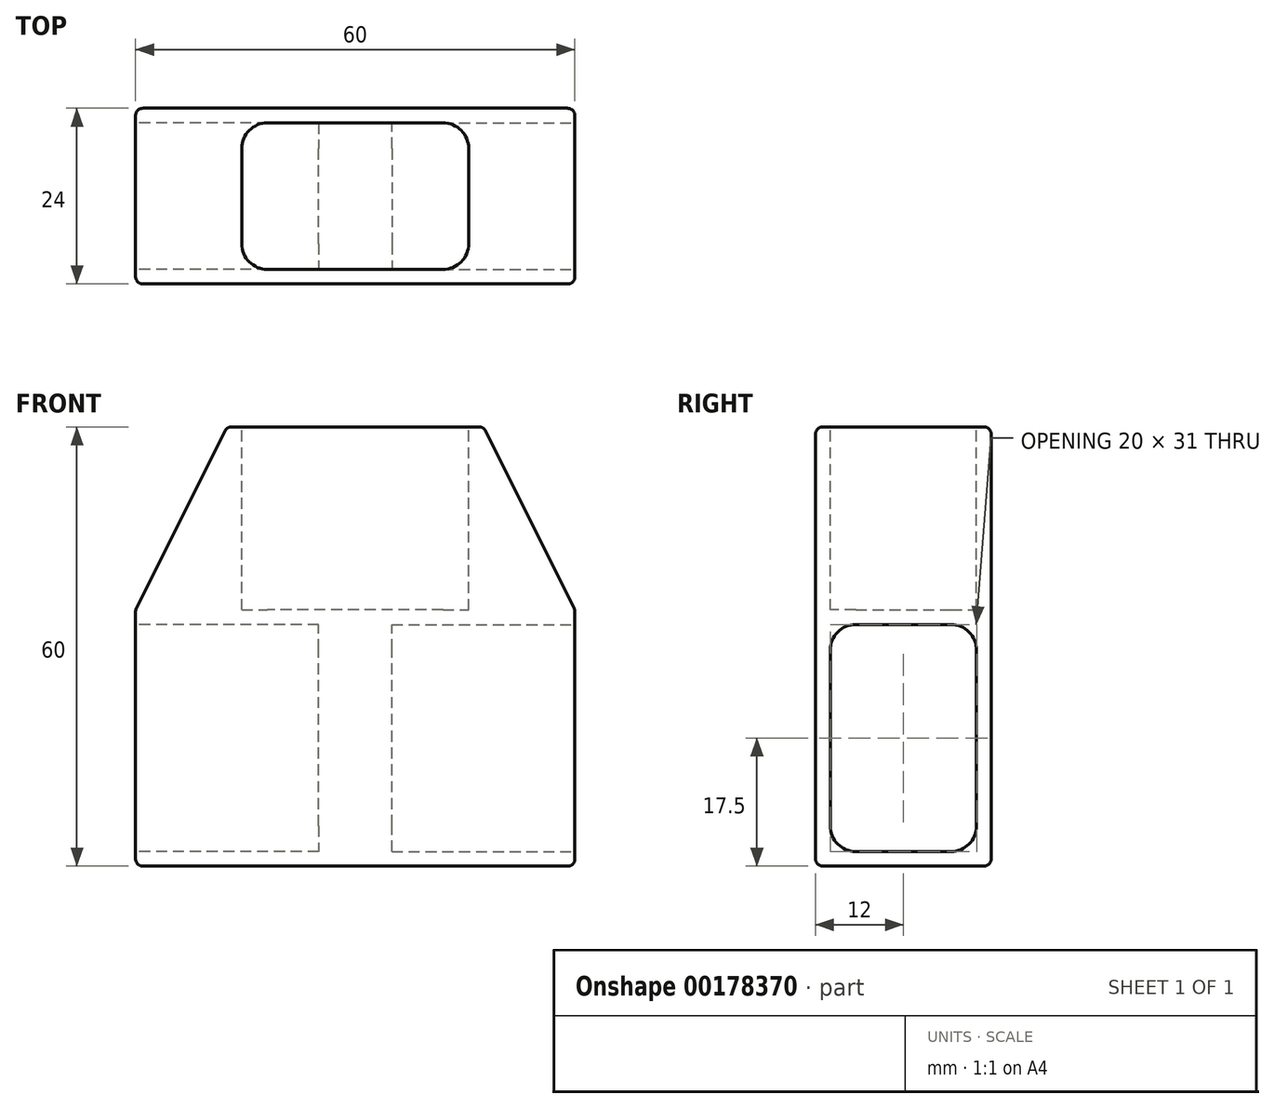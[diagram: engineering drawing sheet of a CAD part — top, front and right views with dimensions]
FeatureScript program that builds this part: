
annotation { "Feature Type Name" : "Feature", "Feature Type Description" : "" }
export const myFeature = defineFeature(function(context is Context, id is Id, definition is map)
    precondition{}
    {
        {
            var Q0;
            Q0=qCreatedBy(makeId("Top.planeOp"),FACE);
            var sketch = newSketch(context, id + "F0", { "sketchPlane" : qUnion([Q0])});
            skLineSegment(sketch, "E0.bottom", {"start": v(30, -12) * mm, "end": v(-30, -12) * mm});
            skLineSegment(sketch, "E0.top", {"start": v(30, 12) * mm, "end": v(-30, 12) * mm});
            skLineSegment(sketch, "E0.left", {"start": v(30, -12) * mm, "end": v(30, 12) * mm});
            skLineSegment(sketch, "E0.right", {"start": v(-30, -12) * mm, "end": v(-30, 12) * mm});
            skPoint(sketch, "E0.middle", {"position": v(0, 0) * mm});
            skSolve(sketch);
        }
        {
            var Q0;
            Q0=makeQuery(id+"F0.imprint","IMPRINT",FACE,{"disambiguationData":[TD([[makeQuery(id+"F0.imprint","IMPRINT",EDGE,{"derivedFrom":sQuery(id+"F0.wireOp",EDGE,"E0.bottom")}),-1.0]])]});
            extrude(context, id + "F1", {"entities" : qUnion([Q0]), "depth" : 60 * mm});
        }
        {
            var Q0;
            Q0=makeQuery(id+"F1.opExtrude","CAP_FACE",FACE,{"disambiguationData":[OSD([sQuery(id+"F0.wireOp",EDGE,"E0.bottom"),sQuery(id+"F0.wireOp",EDGE,"E0.top"),sQuery(id+"F0.wireOp",EDGE,"E0.left"),sQuery(id+"F0.wireOp",EDGE,"E0.right")])],"isStart":false});
            var sketch = newSketch(context, id + "F2", { "sketchPlane" : qUnion([Q0])});
            skLineSegment(sketch, "E1.bottom", {"start": v(15.5, -10) * mm, "end": v(-15.5, -10) * mm});
            skLineSegment(sketch, "E1.top", {"start": v(15.5, 10) * mm, "end": v(-15.5, 10) * mm});
            skLineSegment(sketch, "E1.left", {"start": v(15.5, -10) * mm, "end": v(15.5, 10) * mm});
            skLineSegment(sketch, "E1.right", {"start": v(-15.5, -10) * mm, "end": v(-15.5, 10) * mm});
            skPoint(sketch, "E1.middle", {"position": v(0, 0) * mm});
            skSolve(sketch);
        }
        {
            var Q0;
            Q0=makeQuery(id+"F1.opExtrude","SWEPT_FACE",FACE,{"disambiguationData":[OSD([sQuery(id+"F0.wireOp",EDGE,"E0.left")])]});
            var sketch = newSketch(context, id + "F3", { "sketchPlane" : qUnion([Q0])});
            skLineSegment(sketch, "E2.bottom", {"start": v(10, 2) * mm, "end": v(-10, 2) * mm});
            skLineSegment(sketch, "E2.top", {"start": v(10, 33) * mm, "end": v(-10, 33) * mm});
            skLineSegment(sketch, "E2.left", {"start": v(10, 2) * mm, "end": v(10, 33) * mm});
            skLineSegment(sketch, "E2.right", {"start": v(-10, 2) * mm, "end": v(-10, 33) * mm});
            skPoint(sketch, "E2.middle", {"position": v(0, 17.5) * mm});
            skSolve(sketch);
        }
        {
            var Q0;
            Q0=makeQuery(id+"F1.opExtrude","SWEPT_FACE",FACE,{"disambiguationData":[OSD([sQuery(id+"F0.wireOp",EDGE,"E0.right")])]});
            var sketch = newSketch(context, id + "F4", { "sketchPlane" : qUnion([Q0])});
            skLineSegment(sketch, "E3.bottom", {"start": v(10, 2) * mm, "end": v(-10, 2) * mm});
            skLineSegment(sketch, "E3.top", {"start": v(10, 33) * mm, "end": v(-10, 33) * mm});
            skLineSegment(sketch, "E3.left", {"start": v(10, 2) * mm, "end": v(10, 33) * mm});
            skLineSegment(sketch, "E3.right", {"start": v(-10, 2) * mm, "end": v(-10, 33) * mm});
            skPoint(sketch, "E3.middle", {"position": v(0, 17.5) * mm});
            skSolve(sketch);
        }
        {
            var Q0;
            Q0=makeQuery(id+"F2.imprint","IMPRINT",FACE,{"disambiguationData":[TD([[makeQuery(id+"F2.imprint","IMPRINT",EDGE,{"derivedFrom":sQuery(id+"F2.wireOp",EDGE,"E1.bottom")}),-1.0]])]});
            extrude(context, id + "F5", {"entities" : qUnion([Q0]), "operationType" : NewBodyOperationType.REMOVE, "oppositeDirection" : true, "depth" : 25 * mm});
        }
        {
            var Q0;
            Q0=makeQuery(id+"F4.imprint","IMPRINT",FACE,{"disambiguationData":[TD([[makeQuery(id+"F4.imprint","IMPRINT",EDGE,{"derivedFrom":sQuery(id+"F4.wireOp",EDGE,"E3.bottom")}),-1.0]])]});
            extrude(context, id + "F6", {"entities" : qUnion([Q0]), "operationType" : NewBodyOperationType.REMOVE, "oppositeDirection" : true, "depth" : 25 * mm});
        }
        {
            var Q0;
            Q0=makeQuery(id+"F3.imprint","IMPRINT",FACE,{"disambiguationData":[TD([[makeQuery(id+"F3.imprint","IMPRINT",EDGE,{"derivedFrom":sQuery(id+"F3.wireOp",EDGE,"E2.bottom")}),-1.0]])]});
            extrude(context, id + "F7", {"entities" : qUnion([Q0]), "operationType" : NewBodyOperationType.REMOVE, "oppositeDirection" : true, "depth" : 25 * mm});
        }
        {
            var Q0;
            Q0=makeQuery(id+"F1.opExtrude","CAP_EDGE",EDGE,{"disambiguationData":[OSD([sQuery(id+"F0.wireOp",EDGE,"E0.left")])],"isStart":false});
            var Q1;
            Q1=makeQuery(id+"F1.opExtrude","CAP_EDGE",EDGE,{"disambiguationData":[OSD([sQuery(id+"F0.wireOp",EDGE,"E0.right")])],"isStart":false});
            chamfer(context, id + "F8", {"entities" : qUnion([Q0, Q1]), "chamferType" : ChamferType.TWO_OFFSETS, "width1" : 12.5 * mm, "oppositeDirection" : false, "width2" : 25 * mm, "tangentPropagation" : true});
        }
        {
            var Q0;
            Q0=makeQuery(id+"F6.boolean.opBoolean","COPY",EDGE,{"derivedFrom":makeQuery(id+"F6.opExtrude","SWEPT_EDGE",EDGE,{"disambiguationData":[OSD([sQuery(id+"F4.wireOp",EDGE,"E3.top"),sQuery(id+"F4.wireOp",EDGE,"E3.right")])]})});
            var Q1;
            Q1=makeQuery(id+"F6.boolean.opBoolean","COPY",EDGE,{"derivedFrom":makeQuery(id+"F6.opExtrude","SWEPT_EDGE",EDGE,{"disambiguationData":[OSD([sQuery(id+"F4.wireOp",EDGE,"E3.top"),sQuery(id+"F4.wireOp",EDGE,"E3.left")])]})});
            var Q2;
            Q2=makeQuery(id+"F6.boolean.opBoolean","COPY",EDGE,{"derivedFrom":makeQuery(id+"F6.opExtrude","SWEPT_EDGE",EDGE,{"disambiguationData":[OSD([sQuery(id+"F4.wireOp",EDGE,"E3.bottom"),sQuery(id+"F4.wireOp",EDGE,"E3.left")])]})});
            var Q3;
            Q3=makeQuery(id+"F6.boolean.opBoolean","COPY",EDGE,{"derivedFrom":makeQuery(id+"F6.opExtrude","SWEPT_EDGE",EDGE,{"disambiguationData":[OSD([sQuery(id+"F4.wireOp",EDGE,"E3.bottom"),sQuery(id+"F4.wireOp",EDGE,"E3.right")])]})});
            var Q4;
            Q4=makeQuery(id+"F5.boolean.opBoolean","COPY",EDGE,{"derivedFrom":makeQuery(id+"F5.opExtrude","SWEPT_EDGE",EDGE,{"disambiguationData":[OSD([sQuery(id+"F2.wireOp",EDGE,"E1.bottom"),sQuery(id+"F2.wireOp",EDGE,"E1.left")])]})});
            var Q5;
            Q5=makeQuery(id+"F5.boolean.opBoolean","COPY",EDGE,{"derivedFrom":makeQuery(id+"F5.opExtrude","SWEPT_EDGE",EDGE,{"disambiguationData":[OSD([sQuery(id+"F2.wireOp",EDGE,"E1.top"),sQuery(id+"F2.wireOp",EDGE,"E1.left")])]})});
            var Q6;
            Q6=makeQuery(id+"F5.boolean.opBoolean","COPY",EDGE,{"derivedFrom":makeQuery(id+"F5.opExtrude","SWEPT_EDGE",EDGE,{"disambiguationData":[OSD([sQuery(id+"F2.wireOp",EDGE,"E1.top"),sQuery(id+"F2.wireOp",EDGE,"E1.right")])]})});
            var Q7;
            Q7=makeQuery(id+"F5.boolean.opBoolean","COPY",EDGE,{"derivedFrom":makeQuery(id+"F5.opExtrude","SWEPT_EDGE",EDGE,{"disambiguationData":[OSD([sQuery(id+"F2.wireOp",EDGE,"E1.bottom"),sQuery(id+"F2.wireOp",EDGE,"E1.right")])]})});
            var Q8;
            Q8=makeQuery(id+"F7.boolean.opBoolean","COPY",EDGE,{"derivedFrom":makeQuery(id+"F7.opExtrude","SWEPT_EDGE",EDGE,{"disambiguationData":[OSD([sQuery(id+"F3.wireOp",EDGE,"E2.bottom"),sQuery(id+"F3.wireOp",EDGE,"E2.right")])]})});
            var Q9;
            Q9=makeQuery(id+"F7.boolean.opBoolean","COPY",EDGE,{"derivedFrom":makeQuery(id+"F7.opExtrude","SWEPT_EDGE",EDGE,{"disambiguationData":[OSD([sQuery(id+"F3.wireOp",EDGE,"E2.top"),sQuery(id+"F3.wireOp",EDGE,"E2.right")])]})});
            var Q10;
            Q10=makeQuery(id+"F7.boolean.opBoolean","COPY",EDGE,{"derivedFrom":makeQuery(id+"F7.opExtrude","SWEPT_EDGE",EDGE,{"disambiguationData":[OSD([sQuery(id+"F3.wireOp",EDGE,"E2.top"),sQuery(id+"F3.wireOp",EDGE,"E2.left")])]})});
            var Q11;
            Q11=makeQuery(id+"F7.boolean.opBoolean","COPY",EDGE,{"derivedFrom":makeQuery(id+"F7.opExtrude","SWEPT_EDGE",EDGE,{"disambiguationData":[OSD([sQuery(id+"F3.wireOp",EDGE,"E2.bottom"),sQuery(id+"F3.wireOp",EDGE,"E2.left")])]})});
            fillet(context, id + "F9", {"entities" : qUnion([Q0, Q1, Q2, Q3, Q4, Q5, Q6, Q7, Q8, Q9, Q10, Q11]), "radius" : 3.5 * mm, "tangentPropagation" : true, "allowEdgeOverflow" : false});
        }
        {
            var Q0;
            Q0=makeQuery(id+"F1.opExtrude","SWEPT_FACE",FACE,{"disambiguationData":[OSD([sQuery(id+"F0.wireOp",EDGE,"E0.bottom")])]});
            var Q1;
            Q1=makeQuery(id+"F1.opExtrude","SWEPT_FACE",FACE,{"disambiguationData":[OSD([sQuery(id+"F0.wireOp",EDGE,"E0.top")])]});
            var Q2;
            Q2=makeQuery(id+"F1.opExtrude","CAP_FACE",FACE,{"disambiguationData":[OSD([sQuery(id+"F0.wireOp",EDGE,"E0.bottom"),sQuery(id+"F0.wireOp",EDGE,"E0.top"),sQuery(id+"F0.wireOp",EDGE,"E0.left"),sQuery(id+"F0.wireOp",EDGE,"E0.right")])],"isStart":true});
            var Q3;
            Q3=makeQuery(id+"F8.opChamfer","BLEND_FACE",FACE,{"disambiguationData":[OSD([sQuery(id+"F0.wireOp",EDGE,"E0.right")])]});
            var Q4;
            Q4=makeQuery(id+"F8.opChamfer","BLEND_FACE",FACE,{"disambiguationData":[OSD([sQuery(id+"F0.wireOp",EDGE,"E0.left")])]});
            fillet(context, id + "F10", {"entities" : qUnion([Q0, Q1, Q2, Q3, Q4]), "radius" : 1 * mm, "tangentPropagation" : true, "allowEdgeOverflow" : false});
        }
    });
